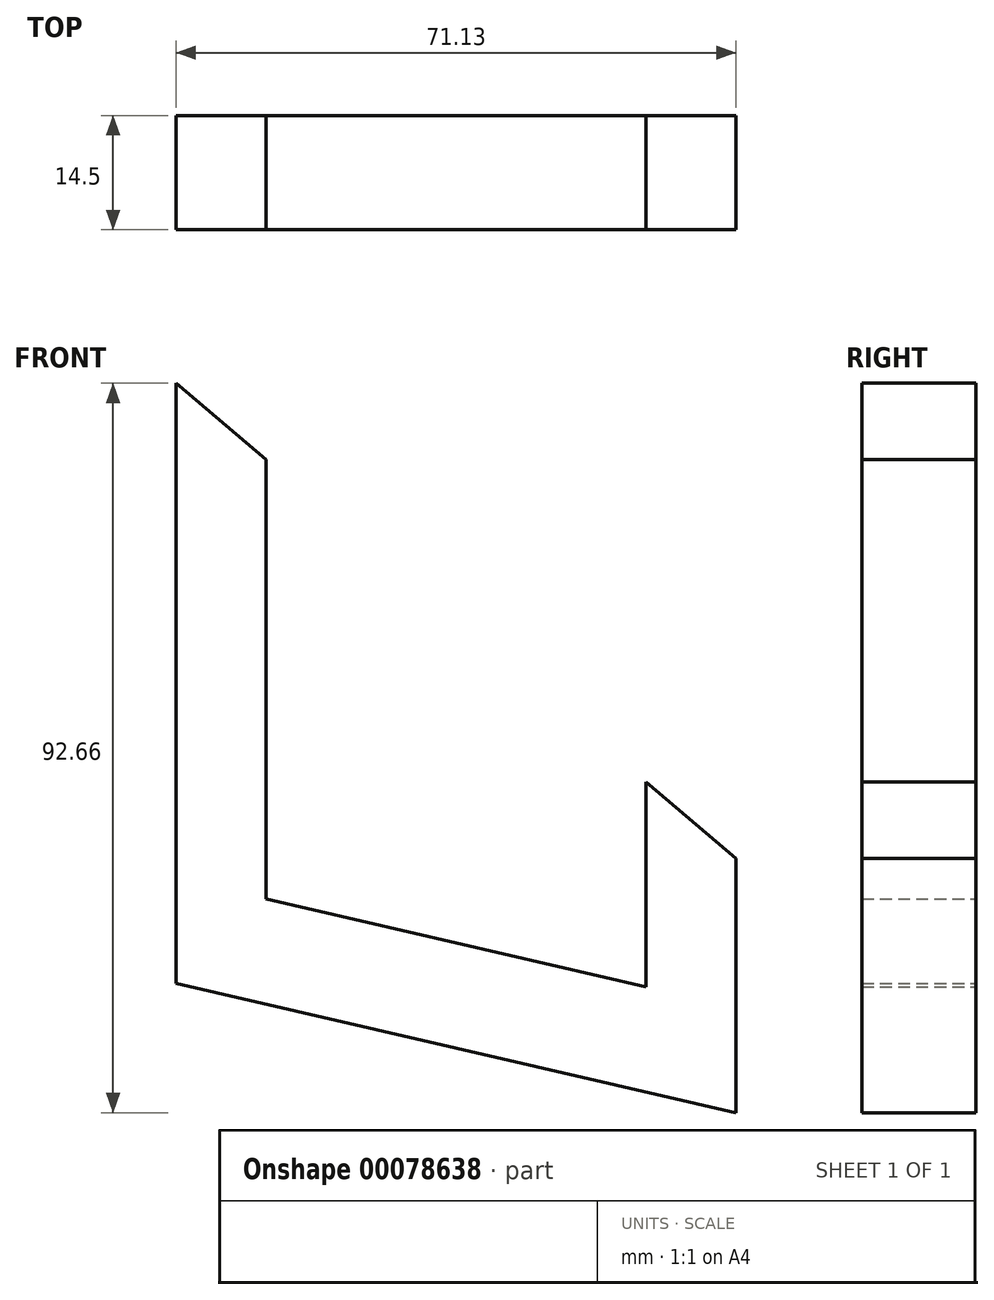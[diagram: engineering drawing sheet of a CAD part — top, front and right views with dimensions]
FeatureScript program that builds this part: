
annotation { "Feature Type Name" : "Feature", "Feature Type Description" : "" }
export const myFeature = defineFeature(function(context is Context, id is Id, definition is map)
    precondition{}
    {
        {
            var Q0;
            Q0=qCreatedBy(makeId("Front.planeOp"),FACE);
            var sketch = newSketch(context, id + "F0", { "sketchPlane" : qUnion([Q0])});
            skLineSegment(sketch, "E0", {"start": v(0, 0) * mm, "end": v(-71.13, 16.42) * mm});
            skLineSegment(sketch, "E1", {"start": v(-71.13, 16.42) * mm, "end": v(-71.13, 92.66) * mm});
            skLineSegment(sketch, "E2", {"start": v(-59.7, 61) * mm, "end": v(-59.7, 27.12) * mm});
            skLineSegment(sketch, "E3", {"start": v(0, 0) * mm, "end": v(0, 32.27) * mm});
            skLineSegment(sketch, "E4", {"start": v(-11.43, 41.98) * mm, "end": v(-11.43, 15.98) * mm});
            skLineSegment(sketch, "E5", {"start": v(-59.7, 27.12) * mm, "end": v(-11.43, 15.98) * mm});
            skLineSegment(sketch, "E6", {"start": v(-71.13, 92.66) * mm, "end": v(-59.7, 82.95) * mm});
            skLineSegment(sketch, "E7", {"start": v(-59.7, 61) * mm, "end": v(-59.7, 82.95) * mm});
            skLineSegment(sketch, "E8.trimOffspring", {"start": v(-11.43, 41.98) * mm, "end": v(0, 32.27) * mm});
            skLineSegment(sketch, "E9", {"start": v(0, 32.27) * mm, "end": v(-86.02, 32.27) * mm, "construction": true});
            skLineSegment(sketch, "E10", {"start": v(-59.7, 82.95) * mm, "end": v(-11.43, 41.98) * mm, "construction": true});
            skSolve(sketch);
        }
        {
            var Q0;
            Q0 = qSketchRegion(id + "F0", true);
            extrude(context, id + "F1", {"entities" : qUnion([Q0]), "depth" : 14.5 * mm});
        }
    });
